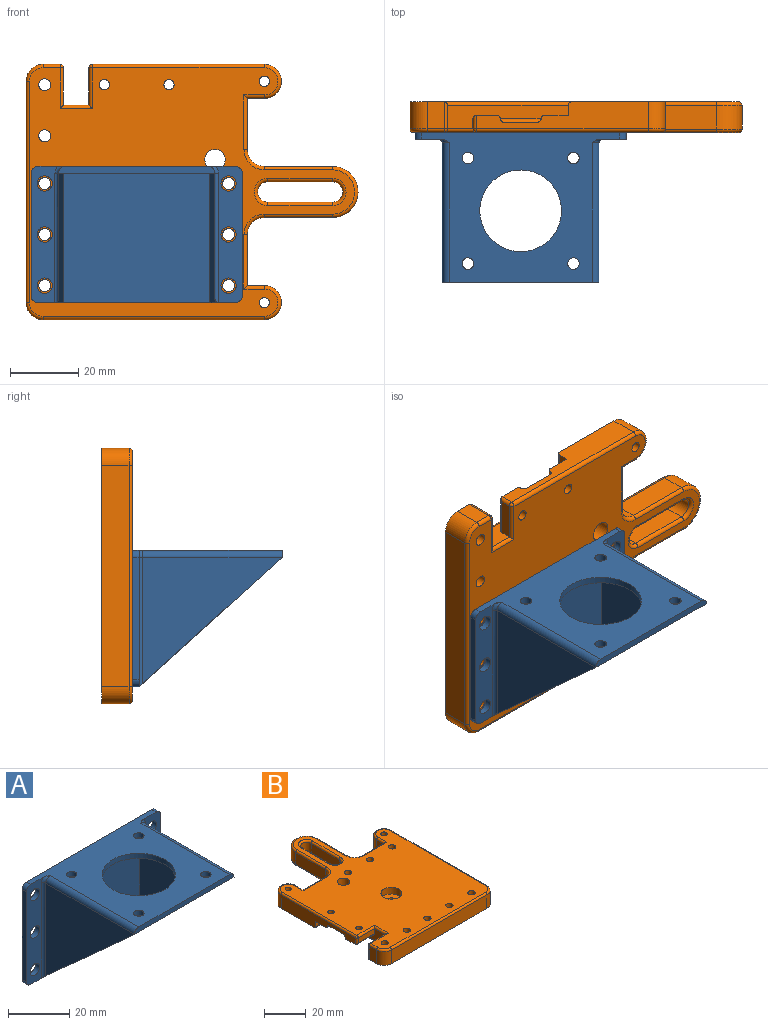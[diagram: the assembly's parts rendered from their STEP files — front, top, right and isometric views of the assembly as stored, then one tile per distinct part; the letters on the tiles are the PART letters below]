
ASSEMBLY  parts=2 mates=1
PART A: 37 faces, bbox 62.4x44.4x42.4 mm
  f0: cylinder r=1mm len=38mm, axis (0,0,1), area 59mm2, adj f1,f3,f10,f26
  f1: torus R=3mm, axis (0,-1,0), area 4.2mm2, adj f0,f2,f8,f10
  f2: cylinder r=2mm len=41mm, axis (0,-1,0), area 128.8mm2, adj f1,f3,f8,f27
  f3: plane 41x37.1mm, normal (-1,0,0), area 760.5mm2, adj f0,f2,f26
  f4: cylinder r=1mm len=38mm, axis (0,0,1), area 59mm2, adj f5,f6,f23,f24
  f5: torus R=3mm, axis (0,-1,0), area 4.2mm2, adj f4,f6,f7,f8
  f6: plane 40x7.76mm, normal (0,-1,0), area 231.1mm2, adj f4,f5,f8,f13,f14,f15,f19,f20
  f7: cylinder r=2mm len=41mm, axis (0,1,0), area 128.8mm2, adj f5,f8,f23,f27
  f8: plane 58.37x44.37mm, normal (0,0,1), area 1392.9mm2, adj f1,f2,f5,f6,f7,f9,f10,f15
  f9: cylinder r=2mm len=2mm, axis (0,-1,0), area 6.3mm2, adj f8,f10,f11,f29
  f10: plane 40x7.76mm, normal (0,-1,0), area 231.1mm2, adj f0,f1,f8,f9,f11,f12,f16,f17
  f11: plane 36x2mm, normal (-1,0,0), area 72mm2, adj f9,f10,f12,f29
  f12: cylinder r=2mm len=2mm, axis (0,1,0), area 6.3mm2, adj f10,f11,f29,f30
  f13: cylinder r=2mm len=2mm, axis (0,-1,0), area 6.3mm2, adj f6,f14,f29,f30
  f14: plane 36x2mm, normal (1,0,0), area 72mm2, adj f6,f13,f15,f29
  f15: cylinder r=2mm len=2mm, axis (0,1,0), area 6.3mm2, adj f6,f8,f14,f29
  f16: cylinder r=2.25mm len=4.5mm, axis (0,-1,0), area 28.3mm2, adj f10,f29
  f17: cylinder r=2.25mm len=4.5mm, axis (0,-1,0), area 28.3mm2, adj f10,f29
  f18: cylinder r=2.25mm len=4.5mm, axis (0,-1,0), area 28.3mm2, adj f10,f29
  f19: cylinder r=2.25mm len=4.5mm, axis (0,1,0), area 28.3mm2, adj f6,f29
  f20: cylinder r=2.25mm len=4.5mm, axis (0,1,0), area 28.3mm2, adj f6,f29
  f21: cylinder r=2.25mm len=4.5mm, axis (0,1,0), area 28.3mm2, adj f6,f29
  f22: plane 42x38mm, normal (-1,0,0), area 798mm2, adj f24,f28,f36
  f23: plane 41x37.1mm, normal (1,0,0), area 760.5mm2, adj f4,f7,f24
  f24: plane 42.38x38.38mm, normal (0,-0.67,-0.74), area 85.2mm2, adj f4,f22,f23,f27,f30
  f25: plane 42x38mm, normal (1,0,0), area 798mm2, adj f26,f28,f36
  f26: plane 42.38x38.38mm, normal (0,-0.67,-0.74), area 85.2mm2, adj f0,f3,f25,f27,f30
  f27: plane 46x2mm, normal (0,-1,0), area 90.3mm2, adj f2,f7,f8,f24,f26,f36
  f28: plane 43x38mm, normal (0,-1,0), area 1634mm2, adj f22,f25,f30,f36
  f29: plane 62x40mm, normal (0,1,0), area 2381.1mm2, adj f8,f9,f11,f12,f13,f14,f15,f16
  f30: plane 58x2mm, normal (0,0,-1), area 116mm2, adj f6,f10,f12,f13,f24,f26,f28,f29
  f31: cylinder r=12mm len=24mm, axis (0,0,1), area 150.8mm2, adj f8,f36
  f32: cylinder r=1.7mm len=3.4mm, axis (0,0,1), area 21.4mm2, adj f8,f36
  f33: cylinder r=1.7mm len=3.4mm, axis (0,0,1), area 21.4mm2, adj f8,f36
  f34: cylinder r=1.7mm len=3.4mm, axis (0,0,1), area 21.4mm2, adj f8,f36
  f35: cylinder r=1.7mm len=3.4mm, axis (0,0,1), area 21.4mm2, adj f8,f36
  f36: plane 43x42mm, normal (0,0,-1), area 1317.3mm2, adj f22,f25,f27,f28,f31,f32,f33,f34
PART B: 102 faces, bbox 75.8x98.5x9 mm
  f0: cylinder r=1.75mm len=5mm, axis (0,0,-1), area 55mm2, adj f5,f100
  f1: plane 15x7mm, normal (0,1,0), area 105mm2, adj f9,f48,f79,f86
  f2: plane 12x7mm, normal (0,0,-1), area 76.9mm2, adj f6,f25,f26,f29,f99
  f3: plane 95.5x73mm, normal (0,0,1), area 4629.9mm2, adj f14,f16,f29,f30,f32,f33,f34,f35
  f4: plane 12x6mm, normal (0,0,-1), area 64.9mm2, adj f6,f25,f30,f53,f95
  f5: plane 96.5x75mm, normal (0,0,-1), area 4550.4mm2, adj f0,f6,f7,f8,f9,f11,f12,f13
  f6: plane 50.5x8mm, normal (-1,0,0), area 271.8mm2, adj f2,f4,f5,f12,f26,f31,f52,f56
  f7: plane 65x8mm, normal (1,0,0), area 520mm2, adj f5,f8,f51,f73
  f8: cylinder r=5mm len=10mm, axis (0,0,-1), area 125.7mm2, adj f5,f7,f9,f75
  f9: plane 8x6mm, normal (-1,0,0), area 40.2mm2, adj f1,f5,f8,f77,f86
  f10: plane 15x7mm, normal (0,1,0), area 105mm2, adj f11,f49,f68,f80
  f11: plane 8x6mm, normal (1,0,0), area 40.2mm2, adj f5,f10,f12,f66,f80
  f12: cylinder r=5mm len=10mm, axis (0,0,-1), area 125.7mm2, adj f5,f6,f11,f64
  f13: plane 8x5mm, normal (-1,0,0), area 40mm2, adj f5,f50,f60,f65
  f14: cylinder r=1.5mm len=9mm, axis (0,0,-1), area 84.8mm2, adj f3,f5
  f15: plane 65x8mm, normal (0,-1,0), area 520mm2, adj f5,f50,f51,f69
  f16: cylinder r=1.5mm len=9mm, axis (0,0,-1), area 84.8mm2, adj f3,f5
  f17: cylinder r=1.75mm len=7mm, axis (0,0,-1), area 77mm2, adj f5,f18
  f18: plane 3.5x3.5mm, normal (0,0,-1), area 9.6mm2, adj f17
  f19: cylinder r=1.75mm len=7mm, axis (0,0,-1), area 77mm2, adj f5,f20
  f20: plane 3.5x3.5mm, normal (0,0,-1), area 9.6mm2, adj f19
  f21: cylinder r=1.75mm len=7mm, axis (0,0,-1), area 77mm2, adj f5,f22
  f22: plane 3.5x3.5mm, normal (0,0,-1), area 9.6mm2, adj f21
  f23: cylinder r=1.75mm len=7mm, axis (0,0,-1), area 77mm2, adj f5,f24
  f24: plane 3.5x3.5mm, normal (0,0,-1), area 9.6mm2, adj f23
  f25: plane 35.5x7mm, normal (-1,0,0), area 149.1mm2, adj f2,f4,f26,f27,f28,f53,f54,f58
  f26: plane 12x3mm, normal (0,-1,0), area 36mm2, adj f2,f6,f25,f52
  f27: plane 11x3mm, normal (0,-1,0), area 33mm2, adj f25,f53,f55,f56
  f28: plane 11x7mm, normal (0,1,0), area 77mm2, adj f25,f57,f60,f61
  f29: cylinder r=1.5mm len=5mm, axis (0,0,-1), area 47.1mm2, adj f2,f3
  f30: cylinder r=1.5mm len=5mm, axis (0,0,-1), area 47.1mm2, adj f3,f4
  f31: plane 11x10mm, normal (0,0,-1), area 110mm2, adj f6,f96,f97,f98
  f32: cylinder r=1.75mm len=9mm, axis (0,0,1), area 99mm2, adj f3,f5
  f33: cylinder r=1.75mm len=9mm, axis (0,0,1), area 99mm2, adj f3,f5
  f34: cylinder r=1.75mm len=9mm, axis (0,0,1), area 99mm2, adj f3,f5
  f35: cylinder r=3mm len=9mm, axis (0,0,1), area 169.6mm2, adj f3,f5
  f36: cylinder r=1.75mm len=9mm, axis (0,0,1), area 99mm2, adj f3,f5
  f37: cylinder r=1.75mm len=9mm, axis (0,0,1), area 99mm2, adj f3,f5
  f38: cylinder r=1.75mm len=9mm, axis (0,0,1), area 99mm2, adj f3,f5
  f39: cylinder r=1.75mm len=9mm, axis (0,0,1), area 99mm2, adj f3,f5
  f40: cylinder r=1.75mm len=9mm, axis (0,0,1), area 99mm2, adj f3,f5
  f41: plane 19x7mm, normal (-1,0,0), area 133mm2, adj f42,f47,f87,f91
  f42: cylinder r=3mm len=7mm, axis (0,0,-1), area 66mm2, adj f41,f43,f88,f92
  f43: plane 19x7mm, normal (1,0,0), area 133mm2, adj f42,f47,f90,f94
  f44: plane 20x7mm, normal (1,0,0), area 140mm2, adj f45,f48,f76,f84
  f45: cylinder r=7.5mm len=15mm, axis (0,0,-1), area 164.9mm2, adj f44,f46,f74,f83
  f46: plane 20x7mm, normal (-1,0,0), area 140mm2, adj f45,f49,f72,f82
  f47: cylinder r=3mm len=7mm, axis (0,0,-1), area 66mm2, adj f41,f43,f89,f93
  f48: cylinder r=5mm len=7mm, axis (0,0,1), area 55mm2, adj f1,f44,f78,f85
  f49: cylinder r=5mm len=7mm, axis (0,0,-1), area 55mm2, adj f10,f46,f70,f81
  f50: cylinder r=5mm len=8mm, axis (0,0,1), area 62.8mm2, adj f5,f13,f15,f67
  f51: cylinder r=5mm len=8mm, axis (0,0,-1), area 62.8mm2, adj f5,f7,f15,f71
  f52: cylinder r=1mm len=13mm, axis (1,0,0), area 19.4mm2, adj f5,f6,f26,f54
  f53: cylinder r=1mm len=12mm, axis (-1,0,0), area 18.3mm2, adj f4,f25,f27,f56
  f54: cylinder r=1mm len=37.5mm, axis (0,-1,0), area 56.9mm2, adj f5,f25,f52,f57
  f55: cylinder r=1mm len=12mm, axis (1,0,0), area 17.8mm2, adj f3,f27,f58,f59
  f56: cylinder r=1mm len=4mm, axis (0,0,-1), area 5.7mm2, adj f6,f27,f53,f59
  f57: cylinder r=1mm len=13mm, axis (-1,0,0), area 18.8mm2, adj f5,f28,f54,f60
  f58: cylinder r=1mm len=9.5mm, axis (0,-1,0), area 12.9mm2, adj f3,f25,f55,f61
  f59: sphere r=1mm, area 1.6mm2, adj f55,f56,f62
  f60: cylinder r=1mm len=8mm, axis (0,0,-1), area 12mm2, adj f13,f28,f57,f63
  f61: cylinder r=1mm len=12mm, axis (-1,0,0), area 17.8mm2, adj f3,f28,f58,f63
  f62: cylinder r=1mm len=50.5mm, axis (0,1,0), area 79.3mm2, adj f3,f6,f59,f64
  f63: sphere r=1mm, area 1.6mm2, adj f60,f61,f65
  f64: torus R=4mm, axis (0,0,1), area 22.9mm2, adj f3,f12,f62,f66
  f65: cylinder r=1mm len=5mm, axis (0,1,0), area 7.9mm2, adj f3,f13,f63,f67
  f66: cylinder r=1mm len=6mm, axis (0,-1,0), area 8.4mm2, adj f3,f11,f64,f68
  f67: torus R=4mm, axis (0,0,1), area 11.4mm2, adj f3,f50,f65,f69
  f68: cylinder r=1mm len=16mm, axis (1,0,0), area 24.1mm2, adj f3,f10,f66,f70
  f69: cylinder r=1mm len=65mm, axis (-1,0,0), area 102.1mm2, adj f3,f15,f67,f71
  f70: torus R=6mm, axis (0,0,1), area 13.2mm2, adj f3,f49,f68,f72
  f71: torus R=4mm, axis (0,0,1), area 11.4mm2, adj f3,f51,f69,f73
  f72: cylinder r=1mm len=20mm, axis (0,1,0), area 31.4mm2, adj f3,f46,f70,f74
  f73: cylinder r=1mm len=65mm, axis (0,-1,0), area 102.1mm2, adj f3,f7,f71,f75
  f74: torus R=6.5mm, axis (0,0,1), area 35.2mm2, adj f3,f45,f72,f76
  f75: torus R=4mm, axis (0,0,1), area 22.9mm2, adj f3,f8,f73,f77
  f76: cylinder r=1mm len=20mm, axis (0,-1,0), area 31.4mm2, adj f3,f44,f74,f78
  f77: cylinder r=1mm len=6mm, axis (0,1,0), area 8.4mm2, adj f3,f9,f75,f79
  f78: torus R=6mm, axis (0,0,1), area 13.2mm2, adj f3,f48,f76,f79
  f79: cylinder r=1mm len=16mm, axis (1,0,0), area 24.1mm2, adj f1,f3,f77,f78
  f80: cylinder r=1mm len=15mm, axis (-1,0,0), area 23.6mm2, adj f5,f10,f11,f81
  f81: torus R=6mm, axis (0,0,1), area 13.2mm2, adj f5,f49,f80,f82
  f82: cylinder r=1mm len=20mm, axis (0,-1,0), area 31.4mm2, adj f5,f46,f81,f83
  f83: torus R=6.5mm, axis (0,0,1), area 35.2mm2, adj f5,f45,f82,f84
  f84: cylinder r=1mm len=20mm, axis (0,1,0), area 31.4mm2, adj f5,f44,f83,f85
  f85: torus R=6mm, axis (0,0,1), area 13.2mm2, adj f5,f48,f84,f86
  f86: cylinder r=1mm len=15mm, axis (-1,0,0), area 23.6mm2, adj f1,f5,f9,f85
  f87: cylinder r=1mm len=19mm, axis (0,-1,0), area 29.8mm2, adj f5,f41,f88,f89
  f88: torus R=4mm, axis (0,0,1), area 16.6mm2, adj f5,f42,f87,f90
  f89: torus R=4mm, axis (0,0,1), area 16.6mm2, adj f5,f47,f87,f90
  f90: cylinder r=1mm len=19mm, axis (0,1,0), area 29.8mm2, adj f5,f43,f88,f89
  f91: cylinder r=1mm len=19mm, axis (0,1,0), area 29.8mm2, adj f3,f41,f92,f93
  f92: torus R=4mm, axis (0,0,1), area 16.6mm2, adj f3,f42,f91,f94
  f93: torus R=4mm, axis (0,0,1), area 16.6mm2, adj f3,f47,f91,f94
  f94: cylinder r=1mm len=19mm, axis (0,-1,0), area 29.8mm2, adj f3,f43,f92,f93
  f95: cylinder r=1mm len=12mm, axis (-1,0,0), area 18.8mm2, adj f4,f6,f25,f96
  f96: cylinder r=1mm len=12mm, axis (-1,0,0), area 18.3mm2, adj f6,f31,f95,f97
  f97: cylinder r=1mm len=12mm, axis (0,-1,0), area 17.7mm2, adj f25,f31,f96,f98
  f98: cylinder r=1mm len=12mm, axis (1,0,0), area 18.3mm2, adj f6,f31,f97,f99
  f99: cylinder r=1mm len=12mm, axis (1,0,0), area 18.8mm2, adj f2,f6,f25,f98
  f100: plane 10x10mm, normal (0,0,1), area 68.9mm2, adj f0,f101
  f101: cylinder r=5mm len=10mm, axis (0,0,1), area 125.7mm2, adj f3,f100
PLACE A t=(-18.18,-32.92,-5.28)mm
PLACE B rot(axis=(0.58,0.58,-0.58),120deg) t=(-18.18,-0.92,-10.78)mm
MATE fastened B.f32 <-> A.f21  axis (0,-1,0) through (8.82,-9.92,-8.28)mm
